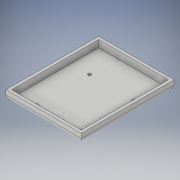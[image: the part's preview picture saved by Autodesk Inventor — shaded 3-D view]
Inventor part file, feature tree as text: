
AUTODESK INVENTOR PART (.ipt)
format: ipt  version: 2019.4 (Build 234330000, 330)  size: 131,584 bytes
history: native  units: mm
features: extrude x3, sketch x3, fillet x1
ambient origin geometry x8: Origin, YZ Plane, XZ Plane, XY Plane, X Axis, Y Axis, Z Axis, Center Point
bodies: Solid1 (feature_tree)
feature tree (7):
  extrude  "Extrusion1"  Depth=96.0mm
  extrude  "Extrusion2"  Depth=10.0mm TaperAngle=0.0deg
  extrude  "Extrusion3"  Depth=96.0mm
  fillet  "Fillet1"  Radius=8.0mm
  sketch  "Sketch1"  dims[d0=77.0mm d1=96.0mm]
  sketch  "Sketch2"  dims[d2=3.0mm d3=10.0mm d4=0.0mm]
  sketch  "Sketch3"  dims[d5=77.0mm d6=96.0mm d7=8.0mm d8=0.0mm d9=7.5mm d10=7.5mm d11=3.5mm d12=20.0mm d14=58.0mm d15=20.0mm d17=49.0mm d20=3.0mm d21=0.0mm d22=5.0mm]
